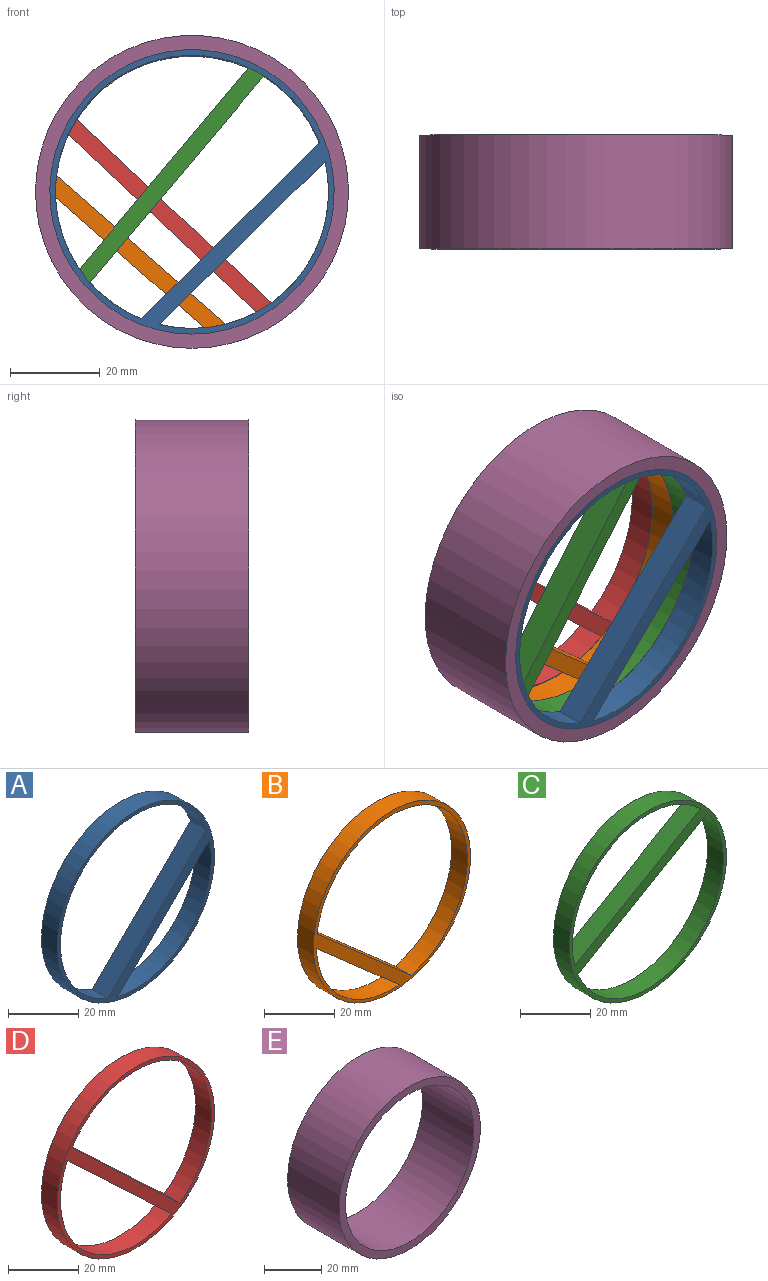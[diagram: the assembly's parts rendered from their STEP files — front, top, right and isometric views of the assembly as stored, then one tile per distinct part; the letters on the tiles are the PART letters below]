
ASSEMBLY  parts=5 mates=8
PART A: 7 faces, bbox 63.5x6.4x63.5 mm
  f0: cylinder r=30.48mm len=37.77mm, axis (0,1,0), area 394.4mm2, adj f4,f5,f6
  f1: cylinder r=30.48mm len=58.93mm, axis (0,1,0), area 767.1mm2, adj f2,f5,f6
  f2: plane 39.83x39.2mm, normal (-0.7,0,0.71), area 354.9mm2, adj f1,f5,f6
  f3: cylinder r=31.75mm len=63.5mm, axis (0,1,0), area 1266.8mm2, adj f5,f6
  f4: plane 36.99x36.41mm, normal (0.7,0,-0.71), area 329.6mm2, adj f0,f5,f6
  f5: plane 63.5x63.5mm, normal (0,-1,0), area 454.1mm2, adj f0,f1,f2,f3,f4
  f6: plane 63.5x63.5mm, normal (0,1,0), area 454.1mm2, adj f0,f1,f2,f3,f4
PART B: 7 faces, bbox 63.5x6.4x63.5 mm
  f0: cylinder r=30.48mm len=33.42mm, axis (0,1,0), area 316.8mm2, adj f4,f5,f6
  f1: cylinder r=30.48mm len=60.71mm, axis (0,1,0), area 837.4mm2, adj f2,f5,f6
  f2: plane 37.98x33.39mm, normal (0.66,0,0.75), area 321.1mm2, adj f1,f5,f6
  f3: cylinder r=31.75mm len=63.5mm, axis (0,1,0), area 1266.8mm2, adj f5,f6
  f4: plane 33.42x29.38mm, normal (-0.66,0,-0.75), area 282.6mm2, adj f0,f5,f6
  f5: plane 63.5x63.5mm, normal (0,-1,0), area 430mm2, adj f0,f1,f2,f3,f4
  f6: plane 63.5x63.5mm, normal (0,1,0), area 430mm2, adj f0,f1,f2,f3,f4
PART C: 7 faces, bbox 63.5x6.4x63.5 mm
  f0: plane 52.23x30.22mm, normal (0.5,0,-0.87), area 383.2mm2, adj f4,f5,f6
  f1: cylinder r=30.48mm len=51.82mm, axis (0,1,0), area 503.3mm2, adj f3,f5,f6
  f2: cylinder r=31.75mm len=63.5mm, axis (0,1,0), area 1266.8mm2, adj f5,f6
  f3: plane 50.84x29.42mm, normal (-0.5,0,0.87), area 373mm2, adj f1,f5,f6
  f4: cylinder r=30.48mm len=58.77mm, axis (0,1,0), area 663.3mm2, adj f0,f5,f6
  f5: plane 63.5x63.5mm, normal (0,-1,0), area 475.5mm2, adj f0,f1,f2,f3,f4
  f6: plane 63.5x63.5mm, normal (0,1,0), area 475.5mm2, adj f0,f1,f2,f3,f4
PART D: 7 faces, bbox 63.5x6.4x63.5 mm
  f0: cylinder r=30.48mm len=44.86mm, axis (0,1,0), area 483mm2, adj f4,f5,f6
  f1: cylinder r=30.48mm len=56.26mm, axis (0,1,0), area 683mm2, adj f2,f5,f6
  f2: plane 43.5x41.06mm, normal (0.69,0,0.73), area 379.9mm2, adj f1,f5,f6
  f3: cylinder r=31.75mm len=63.5mm, axis (0,1,0), area 1266.8mm2, adj f5,f6
  f4: plane 42.04x39.68mm, normal (-0.69,0,-0.73), area 367.1mm2, adj f0,f5,f6
  f5: plane 63.5x63.5mm, normal (0,-1,0), area 472.7mm2, adj f0,f1,f2,f3,f4
  f6: plane 63.5x63.5mm, normal (0,1,0), area 472.7mm2, adj f0,f1,f2,f3,f4
PART E: 4 faces, bbox 69.9x25.4x69.9 mm
  f0: cylinder r=31.75mm len=63.5mm, axis (0,1,0), area 5067.1mm2, adj f2,f3
  f1: cylinder r=34.92mm len=69.85mm, axis (0,1,0), area 5573.8mm2, adj f2,f3
  f2: plane 69.85x69.85mm, normal (0,-1,0), area 665.1mm2, adj f0,f1
  f3: plane 69.85x69.85mm, normal (0,1,0), area 665.1mm2, adj f0,f1
PLACE A t=(-44.99,-36.42,15)mm
PLACE B t=(-44.99,-23.72,14.77)mm
PLACE C rot(axis=(0,-1,0),19.9deg) t=(-44.99,-30.07,15)mm
PLACE D t=(-44.99,-17.37,15)mm
PLACE E t=(-44.99,-17.37,15)mm fixed
MATE cylindrical E.f0 <-> A.f3  axis (0,1,0) through (-44.99,-30.07,15)mm
MATE cylindrical B.f3 <-> E.f0  axis (0,1,0) through (-44.99,-26.9,15)mm
MATE planar B.f5 <-> C.f6  axis (0,-1,0) through (-50.26,-30.07,10.46)mm
MATE cylindrical C.f2 <-> E.f0  axis (0,1,0) through (-44.99,-33.25,15)mm
MATE cylindrical D.f3 <-> E.f0  axis (0,1,0) through (-44.99,-20.55,15)mm
MATE planar D.f5 <-> B.f6  axis (0,-1,0) through (-47.52,-23.72,12.32)mm
MATE planar C.f5 <-> A.f6  axis (0,-1,0) through (-47.27,-36.42,16.92)mm
MATE planar A.f5 <-> E.f1  axis (0,-1,0) through (-40.52,-42.77,10.46)mm
